# Revit family: QF_Brema_FRESHMAKER
name_source: partatom
category: Specialty Equipment
revit_build: Autodesk Revit MEP 2012 (Build: 20110916_2132(x64)
units: mm (PartAtom-declared; Revit-internal decimal feet)

## types (1)
- FRESHMAKER
    Apparent Power = 320 VA
    Assembly Code = E1090320
    BTUH = 0 W
    Cold Water Connection Height = 215 mm
    Cold Water Maximum Pressure = 6.0 bar
    Cold Water Minimum Pressure = 1.0 bar
    Cold Water Size = 1"
    Cold Water Size Radius = 1/2"
    Conn Conduit = Yes
    Cycle = 50 Hz
    Depth = 430 mm  [stored 1.41076 ft]
    Description = AUTOMATIC ICE CUBE MAKER WATER COOLED
    Elec Conn Connection Height = 40 mm  [stored 0.131234 ft]
    FL Amps = 0 A
    Height = 435 mm  [stored 1.42717 ft]
    Indirect Waste Connection Height = 40 mm  [stored 0.131234 ft]
    Indirect Waste Radius = 1/2"
    Indirect Waste Size = 1"
    Manufacturer = BREMA
    Max Overcurrent Protection = 10 A
    Min Ckt Ampacity = 0 A
    Model = FRESHMAKER
    Phase = 1
    Refrigerant Type = R404A
    URL = www.bremaice.it
    Volts = 230 V
    Watts = 320 W
    Weight = 37.5 kg
    Width = 540 mm  [stored 1.77165 ft]

note: [stored X ft] marks values corroborated as IEEE doubles in the binary element streams (Revit-internal decimal feet)

## geometry (parser evidence)
native form markers: Blend x7, Sweep x2
no freeform markers — native parametric forms only
